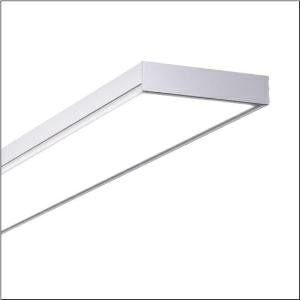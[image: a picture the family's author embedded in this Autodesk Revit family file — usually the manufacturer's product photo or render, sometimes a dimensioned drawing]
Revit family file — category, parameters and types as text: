
# Revit family: apollon_31_surface_51mp26wd2441ea
name_source: partatom
category: Lighting Fixtures
units: mm (PartAtom-declared; Revit-internal decimal feet)

## family parameters
Cut with Voids When Loaded = No
Host = Face
Light Source = No
Part Type = Normal
Room Calculation Point = No
Round Connector Dimension = Use Diameter
Shared = No

## types (1)
- Apollon 31 Surface (1 x LED, 4600 lm, 33 W, 4000K)
    Apparent Load = 33 VA
    CIE Flux Codes = 61 87 97 97 100
    Color Rendering = 80
    Color Temperature = 4000K
    Default Elevation = 1800 mm
    Description = Apollon 31 Surface, office luminaire, primary optical cover: micro prismatic cover, of PMMA, light emission: direct distribution, primary light characteristic: symmetric, installation type: surface-mounted, LED, rated luminous flux: 4.600lm, luminous efficacy: 139lm/W, light colour: 840, colour temperature: 4000K, control gear: DALI 2, with terminal, 5-pole, mains connection: 220..240V, AC, 50/60Hz, rated input power: 33W, housing, of sheet steel, coated, metallic grey (RAL 9006), length: 1.545mm, width: 200mm, height: 44mm, protection rating (complete): IP20, protection rating (on room side): IP40, protection rating (lamp compartment, on room side): IP40, insulation class (complete): insulation class I (protective earthing), certification: CE, ENEC, UKCA, impact resistance: IK02, permissible operating ambient temperature: -20..+40°C, standard: EN 60598-2-22, packaging unit: 1 piece
    Height = 44 mm
    Lamp = 1 x LED
    Lamp Light Flux = 4600 lm
    Lamp Power = 33 W
    Lamp count = 1
    Length = 1545 mm
    Luminous efficacy = 139 lm/W
    Manufacturer = Siteco
    ModVariant = No
    Model = 51MP26WD2441EA
    Mounting Place = Ceiling
    Mounting Type = Surface mounted
    Number of Poles = 1
    OnlyDefault = Yes
    Power Factor = 1
    Product Name = Apollon 31 Surface
    Product group = office luminaire | ceiling mounted
    ProductGroupID = 301
    Protection Class = Protection class I
    Protection Degree = IP 20
    RLX_Detail_Level = 1
    RLX_Emergency_Light_Flux = 0 lm
    RLX_Emergency_Type = 0
    RLX_Emergency_Type_DB = No
    RlxData = <blob elided: 24189 chars, md5=c8520745>
    Socket = socket
    Standby Power = 0 W
    System Light Flux = 4600 lm
    System Power = 33 W
    Type Comments = Product without accessories
    Type Image = l_1313654.jpg
    URL = http://relux.com
    VarID = ---
    Voltage = 0 V
    Weight = 0.00 kg
    Width = 200 mm  [stored 0.656168 ft]

note: [stored X ft] marks values corroborated as IEEE doubles in the binary element streams (Revit-internal decimal feet)

## geometry (parser evidence)
native form markers: Blend x4, Sweep x10
no freeform markers — native parametric forms only
